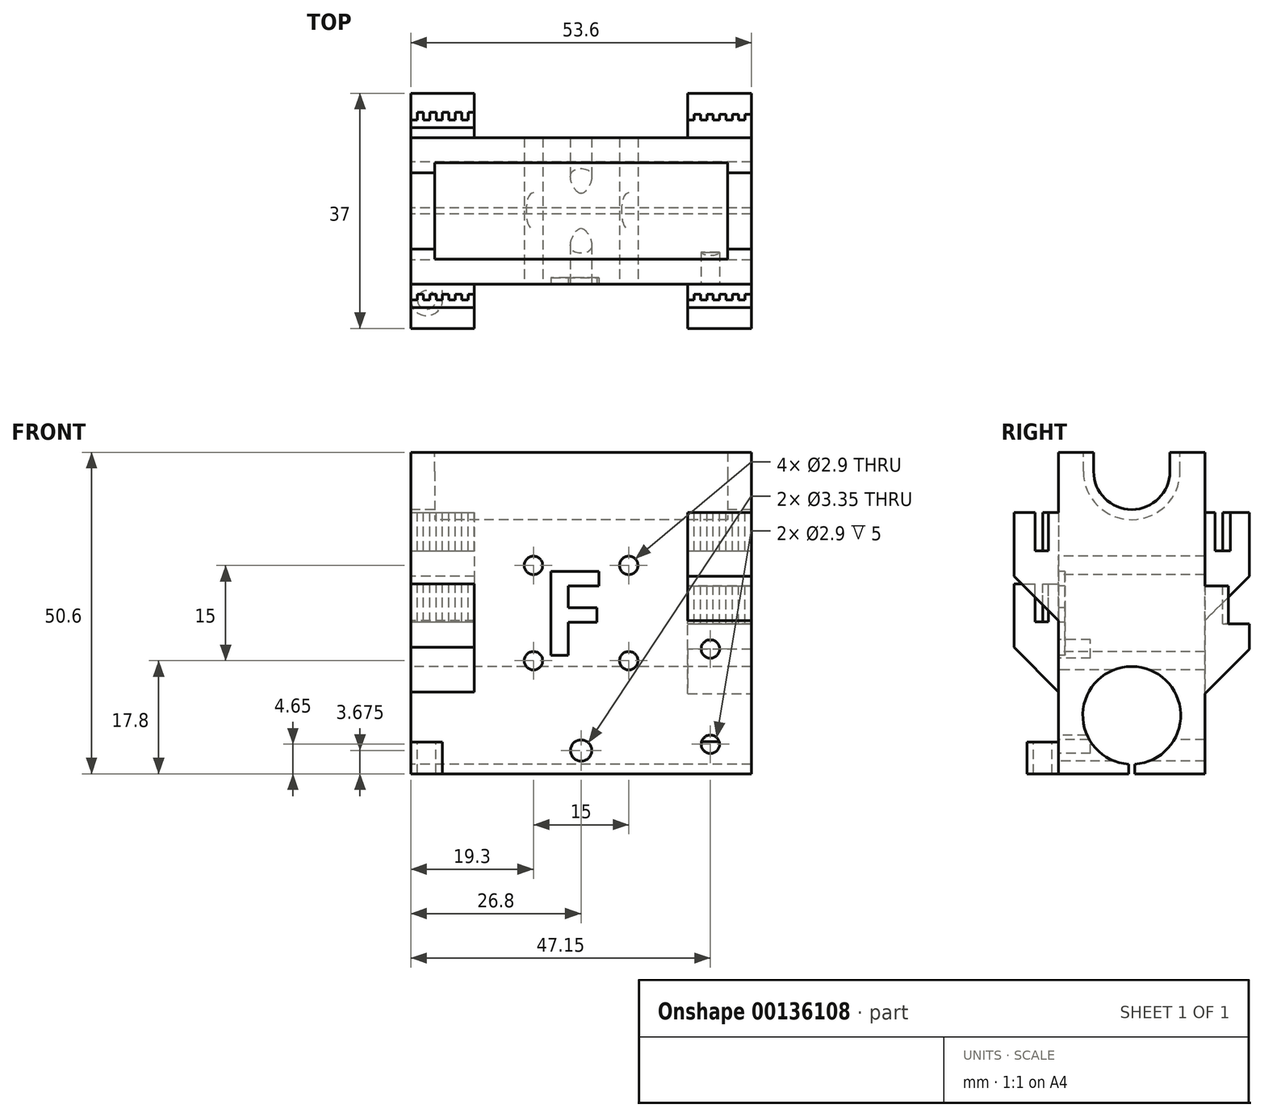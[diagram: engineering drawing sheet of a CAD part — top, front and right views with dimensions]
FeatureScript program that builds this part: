
annotation { "Feature Type Name" : "Feature", "Feature Type Description" : "" }
export const myFeature = defineFeature(function(context is Context, id is Id, definition is map)
    precondition{}
    {
        {
            assignVariable(context, id + "F0", {"name" : "LM8LUU", "anyValue" : 1.8});
        }
        {
            var Q0;
            Q0=qCreatedBy(makeId("Top.planeOp"),FACE);
            var sketch = newSketch(context, id + "F1", { "sketchPlane" : qUnion([Q0])});
            skLineSegment(sketch, "E0.bottom", {"start": v(0, 0) * mm, "end": v(53.6, 0) * mm});
            skLineSegment(sketch, "E0.top", {"start": v(0, 23) * mm, "end": v(53.6, 23) * mm});
            skLineSegment(sketch, "E0.left", {"start": v(0, 0) * mm, "end": v(0, 23) * mm});
            skLineSegment(sketch, "E0.right", {"start": v(53.6, 0) * mm, "end": v(53.6, 23) * mm});
            skSolve(sketch);
        }
        {
            var Q0;
            Q0=qSketchRegion(id+"F1",true);
            extrude(context, id + "F2", {"entities" : qUnion([Q0]), "depth" : 50.6 * mm});
        }
        {
            var Q0;
            Q0=makeQuery(id+"F2.opExtrude","SWEPT_FACE",FACE,{"disambiguationData":[OSD([sQuery(id+"F1.wireOp",EDGE,"E0.left")])]});
            var sketch = newSketch(context, id + "F3", { "sketchPlane" : qUnion([Q0])});
            skCircle(sketch, "E1", {"center": v(-11.5, 9.2) * mm, "radius": 7.7 * mm});
            skCircle(sketch, "E2", {"center": v(-11.5, 47.6) * mm, "radius": 6 * mm});
            skLineSegment(sketch, "E3", {"start": v(-23, 47.6) * mm, "end": v(0, 47.6) * mm, "construction": true});
            skLineSegment(sketch, "E4", {"start": v(-17.5, 50.6) * mm, "end": v(-17.5, 47.6) * mm});
            skLineSegment(sketch, "E5", {"start": v(-5.5, 50.6) * mm, "end": v(-5.5, 47.6) * mm});
            skLineSegment(sketch, "E6", {"start": v(-23, 9.2) * mm, "end": v(0, 9.2) * mm, "construction": true});
            skLineSegment(sketch, "E7", {"start": v(-11.5, 9.2) * mm, "end": v(-11.5, 0) * mm, "construction": true});
            skLineSegment(sketch, "E8", {"start": v(-11.5, 0) * mm, "end": v(-12, 0) * mm});
            skLineSegment(sketch, "E9", {"start": v(-12, 0) * mm, "end": v(-12, 1.52) * mm});
            skLineSegment(sketch, "E10", {"start": v(-12, 1.52) * mm, "end": v(-11, 1.52) * mm});
            skLineSegment(sketch, "E11", {"start": v(-11, 1.52) * mm, "end": v(-11, 0) * mm});
            skLineSegment(sketch, "E12", {"start": v(-11, 0) * mm, "end": v(-11.5, 0) * mm});
            skLineSegment(sketch, "E13", {"start": v(-11.5, 15.6) * mm, "end": v(-11.5, 16.9) * mm});
            skLineSegment(sketch, "E14", {"start": v(-11.5, 15.6) * mm, "end": v(-6.94, 15.4) * mm});
            skLineSegment(sketch, "E15", {"start": v(-11.5, 15.6) * mm, "end": v(-16.06, 15.4) * mm});
            skCircle(sketch, "E16", {"center": v(-11.5, 47.6) * mm, "radius": 7.6 * mm});
            skLineSegment(sketch, "E17", {"start": v(-3.9, 47.6) * mm, "end": v(-3.9, 50.6) * mm});
            skLineSegment(sketch, "E18", {"start": v(-19.1, 47.6) * mm, "end": v(-19.1, 50.6) * mm});
            skSolve(sketch);
        }
        {
            var Q0;
            {var subQ0=sQuery(id+"F3.wireOp",EDGE,"E14");var subQ1=sQuery(id+"F3.wireOp",EDGE,"E1");var subQ3=makeQuery(id+"F3.imprint","INTERSECT",VERTEX,{"disambiguationData":[OD(0.0)],"derivedFrom":[subQ1,subQ0]});Q0=makeQuery(id+"F3.imprint","IMPRINT",FACE,{"disambiguationData":[TD([[makeQuery(id+"F3.imprint","IMPRINT",EDGE,{"disambiguationData":[TD([[subQ3,-1.0]])],"derivedFrom":subQ1}),1.0]])]});}
            var Q1;
            {var subQ0=sQuery(id+"F3.wireOp",EDGE,"E15");var subQ1=sQuery(id+"F3.wireOp",EDGE,"E1");var subQ3=makeQuery(id+"F3.imprint","INTERSECT",VERTEX,{"disambiguationData":[OD(0.0)],"derivedFrom":[subQ1,subQ0]});Q1=makeQuery(id+"F3.imprint","IMPRINT",FACE,{"disambiguationData":[TD([[makeQuery(id+"F3.imprint","IMPRINT",EDGE,{"disambiguationData":[TD([[subQ3,1.0]])],"derivedFrom":subQ1}),1.0]])]});}
            var Q2;
            Q2=makeQuery(id+"F3.imprint","IMPRINT",FACE,{"disambiguationData":[TD([[makeQuery(id+"F3.imprint","IMPRINT",EDGE,{"derivedFrom":sQuery(id+"F3.wireOp",EDGE,"E8")}),-1.0]])]});
            var Q3;
            {var subQ0=sQuery(id+"F3.wireOp",EDGE,"E10");Q3=makeQuery(id+"F3.imprint","IMPRINT",FACE,{"disambiguationData":[TD([[makeQuery(id+"F3.imprint","IMPRINT",EDGE,{"derivedFrom":subQ0}),-1.0]])]});}
            var Q4;
            {var subQ3=sQuery(id+"F3.wireOp",EDGE,"E13");Q4=makeQuery(id+"F3.imprint","IMPRINT",FACE,{"disambiguationData":[TD([[makeQuery(id+"F3.imprint","IMPRINT",EDGE,{"derivedFrom":subQ3}),-1.0]])]});}
            var Q5;
            {var subQ3=sQuery(id+"F3.wireOp",EDGE,"E13");Q5=makeQuery(id+"F3.imprint","IMPRINT",FACE,{"disambiguationData":[TD([[makeQuery(id+"F3.imprint","IMPRINT",EDGE,{"derivedFrom":subQ3}),1.0]])]});}
            var Q6;
            {var subQ7=sQuery(id+"F3.wireOp",EDGE,"E10");Q6=makeQuery(id+"F3.imprint","IMPRINT",FACE,{"disambiguationData":[TD([[makeQuery(id+"F3.imprint","IMPRINT",EDGE,{"derivedFrom":subQ7}),1.0]])]});}
            var Q7;
            {var subQ3=sQuery(id+"F3.wireOp",EDGE,"E5");Q7=makeQuery(id+"F3.imprint","IMPRINT",FACE,{"disambiguationData":[TD([[makeQuery(id+"F3.imprint","IMPRINT",EDGE,{"derivedFrom":subQ3}),-1.0]])]});}
            var Q8;
            {var subQ0=sQuery(id+"F3.wireOp",EDGE,"E4");Q8=makeQuery(id+"F3.imprint","IMPRINT",FACE,{"disambiguationData":[TD([[makeQuery(id+"F3.imprint","IMPRINT",EDGE,{"derivedFrom":subQ0}),1.0]])]});}
            var Q9;
            {var subQ0=sQuery(id+"F3.wireOp",EDGE,"E4");Q9=makeQuery(id+"F3.imprint","IMPRINT",FACE,{"disambiguationData":[TD([[makeQuery(id+"F3.imprint","IMPRINT",EDGE,{"derivedFrom":subQ0}),1.0]])]});}
            var Q10;
            {var subQ3=sQuery(id+"F3.wireOp",EDGE,"E5");Q10=makeQuery(id+"F3.imprint","IMPRINT",FACE,{"disambiguationData":[TD([[makeQuery(id+"F3.imprint","IMPRINT",EDGE,{"derivedFrom":subQ3}),-1.0]])]});}
            var Q11;
            {var subQ1=sQuery(id+"F3.wireOp",EDGE,"E2");var subQ4=makeQuery(id+"F3.imprint","INTERSECT",VERTEX,{"derivedFrom":[subQ1,sQuery(id+"F3.wireOp",EDGE,"E5")]});Q11=makeQuery(id+"F3.imprint","IMPRINT",FACE,{"disambiguationData":[TD([[makeQuery(id+"F3.imprint","IMPRINT",EDGE,{"disambiguationData":[TD([[subQ4,-1.0]])],"derivedFrom":subQ1}),1.0]])]});}
            extrude(context, id + "F4", {"entities" : qUnion([Q0, Q1, Q2, Q3, Q4, Q5, Q6, Q7, Q8, Q9, Q10, Q11]), "operationType" : NewBodyOperationType.REMOVE, "endBound" : BoundingType.THROUGH_ALL, "oppositeDirection" : true, "depth" : 25 * mm});
        }
        {
            var Q0;
            {var subQ3=sQuery(id+"F3.wireOp",EDGE,"E4");Q0=makeQuery(id+"F3.imprint","IMPRINT",FACE,{"disambiguationData":[TD([[makeQuery(id+"F3.imprint","IMPRINT",EDGE,{"derivedFrom":subQ3}),-1.0]])]});}
            var Q1;
            {var subQ3=sQuery(id+"F3.wireOp",EDGE,"E18");Q1=makeQuery(id+"F3.imprint","IMPRINT",FACE,{"disambiguationData":[TD([[makeQuery(id+"F3.imprint","IMPRINT",EDGE,{"derivedFrom":subQ3}),-1.0]])]});}
            var Q2;
            {var subQ3=sQuery(id+"F3.wireOp",EDGE,"E17");Q2=makeQuery(id+"F3.imprint","IMPRINT",FACE,{"disambiguationData":[TD([[makeQuery(id+"F3.imprint","IMPRINT",EDGE,{"derivedFrom":subQ3}),1.0]])]});}
            extrude(context, id + "F5", {"entities" : qUnion([Q0, Q1, Q2]), "operationType" : NewBodyOperationType.REMOVE, "oppositeDirection" : true, "depth" : (46.25 + getVariable(context, 'LM8LUU') * 2) * mm});
        }
        {
            var Q0;
            {var subQ3=sQuery(id+"F3.wireOp",EDGE,"E4");Q0=makeQuery(id+"F3.imprint","IMPRINT",FACE,{"disambiguationData":[TD([[makeQuery(id+"F3.imprint","IMPRINT",EDGE,{"derivedFrom":subQ3}),-1.0]])]});}
            var Q1;
            {var subQ3=sQuery(id+"F3.wireOp",EDGE,"E18");Q1=makeQuery(id+"F3.imprint","IMPRINT",FACE,{"disambiguationData":[TD([[makeQuery(id+"F3.imprint","IMPRINT",EDGE,{"derivedFrom":subQ3}),-1.0]])]});}
            var Q2;
            {var subQ3=sQuery(id+"F3.wireOp",EDGE,"E17");Q2=makeQuery(id+"F3.imprint","IMPRINT",FACE,{"disambiguationData":[TD([[makeQuery(id+"F3.imprint","IMPRINT",EDGE,{"derivedFrom":subQ3}),1.0]])]});}
            extrude(context, id + "F6", {"entities" : qUnion([Q0, Q1, Q2]), "operationType" : NewBodyOperationType.ADD, "oppositeDirection" : true, "depth" : (26.75 - getVariable(context, 'LM8LUU')) * mm});
        }
        {
            var Q0;
            {var subQ3=sQuery(id+"F3.wireOp",EDGE,"E4");Q0=makeQuery(id+"F3.imprint","IMPRINT",FACE,{"disambiguationData":[TD([[makeQuery(id+"F3.imprint","IMPRINT",EDGE,{"derivedFrom":subQ3}),-1.0]])]});}
            var Q1;
            {var subQ3=sQuery(id+"F3.wireOp",EDGE,"E18");Q1=makeQuery(id+"F3.imprint","IMPRINT",FACE,{"disambiguationData":[TD([[makeQuery(id+"F3.imprint","IMPRINT",EDGE,{"derivedFrom":subQ3}),-1.0]])]});}
            var Q2;
            {var subQ3=sQuery(id+"F3.wireOp",EDGE,"E17");Q2=makeQuery(id+"F3.imprint","IMPRINT",FACE,{"disambiguationData":[TD([[makeQuery(id+"F3.imprint","IMPRINT",EDGE,{"derivedFrom":subQ3}),1.0]])]});}
            extrude(context, id + "F7", {"entities" : qUnion([Q0, Q1, Q2]), "operationType" : NewBodyOperationType.REMOVE, "oppositeDirection" : true, "depth" : (23.25 + getVariable(context, 'LM8LUU')) * mm});
        }
        {
            var Q0;
            {var subQ3=sQuery(id+"F3.wireOp",EDGE,"E4");Q0=makeQuery(id+"F3.imprint","IMPRINT",FACE,{"disambiguationData":[TD([[makeQuery(id+"F3.imprint","IMPRINT",EDGE,{"derivedFrom":subQ3}),-1.0]])]});}
            var Q1;
            {var subQ3=sQuery(id+"F3.wireOp",EDGE,"E18");Q1=makeQuery(id+"F3.imprint","IMPRINT",FACE,{"disambiguationData":[TD([[makeQuery(id+"F3.imprint","IMPRINT",EDGE,{"derivedFrom":subQ3}),-1.0]])]});}
            var Q2;
            {var subQ3=sQuery(id+"F3.wireOp",EDGE,"E17");Q2=makeQuery(id+"F3.imprint","IMPRINT",FACE,{"disambiguationData":[TD([[makeQuery(id+"F3.imprint","IMPRINT",EDGE,{"derivedFrom":subQ3}),1.0]])]});}
            extrude(context, id + "F8", {"entities" : qUnion([Q0, Q1, Q2]), "operationType" : NewBodyOperationType.ADD, "oppositeDirection" : true, "depth" : 3.75 * mm});
        }
        {
            var Q0;
            Q0=makeQuery(id+"F2.opExtrude","SWEPT_FACE",FACE,{"disambiguationData":[OSD([sQuery(id+"F1.wireOp",EDGE,"E0.bottom")])]});
            var sketch = newSketch(context, id + "F9", { "sketchPlane" : qUnion([Q0])});
            skLineSegment(sketch, "E19.bottom", {"start": v(0, 29.9) * mm, "end": v(10, 29.9) * mm});
            skLineSegment(sketch, "E19.top", {"start": v(0, 9.9) * mm, "end": v(10, 9.9) * mm});
            skLineSegment(sketch, "E19.left", {"start": v(0, 29.9) * mm, "end": v(0, 9.9) * mm});
            skLineSegment(sketch, "E19.right", {"start": v(10, 29.9) * mm, "end": v(10, 9.9) * mm});
            skLineSegment(sketch, "E20.bottom", {"start": v(53.6, 41.1) * mm, "end": v(43.6, 41.1) * mm});
            skLineSegment(sketch, "E20.top", {"start": v(53.6, 21.1) * mm, "end": v(43.6, 21.1) * mm});
            skLineSegment(sketch, "E20.left", {"start": v(53.6, 41.1) * mm, "end": v(53.6, 21.1) * mm});
            skLineSegment(sketch, "E20.right", {"start": v(43.6, 41.1) * mm, "end": v(43.6, 21.1) * mm});
            skPoint(sketch, "E21", {"position": v(0, 47.6) * mm});
            skPoint(sketch, "E22", {"position": v(0, 9.4) * mm});
            skSolve(sketch);
        }
        {
            var Q0;
            Q0=qSketchRegion(id+"F9",true);
            extrude(context, id + "F10", {"entities" : qUnion([Q0]), "operationType" : NewBodyOperationType.ADD, "depth" : 7 * mm});
        }
        {
            var Q0;
            Q0=makeQuery(id+"F10.opExtrude","CAP_EDGE",EDGE,{"disambiguationData":[OSD([sQuery(id+"F9.wireOp",EDGE,"E19.top")])],"isStart":false});
            var Q1;
            Q1=makeQuery(id+"F10.opExtrude","CAP_EDGE",EDGE,{"disambiguationData":[OSD([sQuery(id+"F9.wireOp",EDGE,"E20.top")])],"isStart":false});
            chamfer(context, id + "F11", {"entities" : qUnion([Q0, Q1]), "width" : 10 * mm, "tangentPropagation" : true});
        }
        {
            var Q0;
            Q0=makeQuery(id+"F10.opExtrude","SWEPT_FACE",FACE,{"disambiguationData":[OSD([sQuery(id+"F9.wireOp",EDGE,"E19.bottom")])]});
            var sketch = newSketch(context, id + "F12", { "sketchPlane" : qUnion([Q0])});
            skLineSegment(sketch, "E23.left", {"start": v(0, -3.7) * mm, "end": v(0, -1.6) * mm});
            skLineSegment(sketch, "E24", {"start": v(6, -2.5) * mm, "end": v(7, -2.5) * mm});
            skLineSegment(sketch, "E25", {"start": v(4, -2.5) * mm, "end": v(5, -2.5) * mm});
            skLineSegment(sketch, "E26", {"start": v(0, -2.5) * mm, "end": v(1, -2.5) * mm});
            skLineSegment(sketch, "E27", {"start": v(7, -1.6) * mm, "end": v(8, -1.6) * mm});
            skLineSegment(sketch, "E28", {"start": v(2, -2.5) * mm, "end": v(3, -2.5) * mm});
            skLineSegment(sketch, "E29", {"start": v(3, -1.6) * mm, "end": v(4, -1.6) * mm});
            skLineSegment(sketch, "E30", {"start": v(8, -2.5) * mm, "end": v(9, -2.5) * mm});
            skLineSegment(sketch, "E31", {"start": v(8, -1.6) * mm, "end": v(8, -2.5) * mm});
            skLineSegment(sketch, "E32", {"start": v(9, -2.5) * mm, "end": v(9, -1.6) * mm});
            skLineSegment(sketch, "E33", {"start": v(10, -1.6) * mm, "end": v(10, -2.5) * mm});
            skLineSegment(sketch, "E34", {"start": v(6, -1.6) * mm, "end": v(6, -2.5) * mm});
            skLineSegment(sketch, "E35", {"start": v(2, -1.6) * mm, "end": v(2, -2.5) * mm});
            skLineSegment(sketch, "E36", {"start": v(1, -1.6) * mm, "end": v(2, -1.6) * mm});
            skLineSegment(sketch, "E37", {"start": v(1, -2.5) * mm, "end": v(1, -1.6) * mm});
            skLineSegment(sketch, "E38", {"start": v(9, -1.6) * mm, "end": v(10, -1.6) * mm});
            skLineSegment(sketch, "E39", {"start": v(5, -1.6) * mm, "end": v(6, -1.6) * mm});
            skLineSegment(sketch, "E40", {"start": v(5, -2.5) * mm, "end": v(5, -1.6) * mm});
            skLineSegment(sketch, "E41", {"start": v(3, -2.5) * mm, "end": v(3, -1.6) * mm});
            skLineSegment(sketch, "E42", {"start": v(4, -1.6) * mm, "end": v(4, -2.5) * mm});
            skLineSegment(sketch, "E43", {"start": v(7, -2.5) * mm, "end": v(7, -1.6) * mm});
            skLineSegment(sketch, "E44", {"start": v(0, -1.6) * mm, "end": v(0, -2.5) * mm});
            skLineSegment(sketch, "E45", {"start": v(10, -2.5) * mm, "end": v(10, -3.7) * mm});
            skLineSegment(sketch, "E46", {"start": v(0, -3.7) * mm, "end": v(10, -3.7) * mm});
            skLineSegment(sketch, "E47", {"start": v(5.3, -1.6) * mm, "end": v(5.3, 0) * mm});
            skSolve(sketch);
        }
        {
            var Q0;
            Q0=qSketchRegion(id+"F12",true);
            extrude(context, id + "F13", {"entities" : qUnion([Q0]), "operationType" : NewBodyOperationType.REMOVE, "oppositeDirection" : true, "depth" : 6 * mm});
        }
        {
            var Q0;
            Q0=makeQuery(id+"F10.opExtrude","SWEPT_FACE",FACE,{"disambiguationData":[OSD([sQuery(id+"F9.wireOp",EDGE,"E20.bottom")])]});
            var sketch = newSketch(context, id + "F14", { "sketchPlane" : qUnion([Q0])});
            skLineSegment(sketch, "E48.left", {"start": v(43.6, -3.7) * mm, "end": v(43.6, -1.6) * mm});
            skLineSegment(sketch, "E49", {"start": v(49.6, -2.5) * mm, "end": v(50.6, -2.5) * mm});
            skLineSegment(sketch, "E50", {"start": v(47.6, -2.5) * mm, "end": v(48.6, -2.5) * mm});
            skLineSegment(sketch, "E51", {"start": v(43.6, -2.5) * mm, "end": v(44.6, -2.5) * mm});
            skLineSegment(sketch, "E52", {"start": v(50.6, -1.6) * mm, "end": v(51.6, -1.6) * mm});
            skLineSegment(sketch, "E53", {"start": v(45.6, -2.5) * mm, "end": v(46.6, -2.5) * mm});
            skLineSegment(sketch, "E54", {"start": v(46.6, -1.6) * mm, "end": v(47.6, -1.6) * mm});
            skLineSegment(sketch, "E55", {"start": v(51.6, -2.5) * mm, "end": v(52.6, -2.5) * mm});
            skLineSegment(sketch, "E56", {"start": v(51.6, -1.6) * mm, "end": v(51.6, -2.5) * mm});
            skLineSegment(sketch, "E57", {"start": v(52.6, -2.5) * mm, "end": v(52.6, -1.6) * mm});
            skLineSegment(sketch, "E58", {"start": v(53.6, -1.6) * mm, "end": v(53.6, -2.5) * mm});
            skLineSegment(sketch, "E59", {"start": v(49.6, -1.6) * mm, "end": v(49.6, -2.5) * mm});
            skLineSegment(sketch, "E60", {"start": v(45.6, -1.6) * mm, "end": v(45.6, -2.5) * mm});
            skLineSegment(sketch, "E61", {"start": v(44.6, -1.6) * mm, "end": v(45.6, -1.6) * mm});
            skLineSegment(sketch, "E62", {"start": v(44.6, -2.5) * mm, "end": v(44.6, -1.6) * mm});
            skLineSegment(sketch, "E63", {"start": v(52.6, -1.6) * mm, "end": v(53.6, -1.6) * mm});
            skLineSegment(sketch, "E64", {"start": v(48.6, -1.6) * mm, "end": v(49.6, -1.6) * mm});
            skLineSegment(sketch, "E65", {"start": v(48.6, -2.5) * mm, "end": v(48.6, -1.6) * mm});
            skLineSegment(sketch, "E66", {"start": v(46.6, -2.5) * mm, "end": v(46.6, -1.6) * mm});
            skLineSegment(sketch, "E67", {"start": v(47.6, -1.6) * mm, "end": v(47.6, -2.5) * mm});
            skLineSegment(sketch, "E68", {"start": v(50.6, -2.5) * mm, "end": v(50.6, -1.6) * mm});
            skLineSegment(sketch, "E69", {"start": v(43.6, -1.6) * mm, "end": v(43.6, -2.5) * mm});
            skLineSegment(sketch, "E70", {"start": v(53.6, -2.5) * mm, "end": v(53.6, -3.7) * mm});
            skLineSegment(sketch, "E71", {"start": v(43.6, -3.7) * mm, "end": v(53.6, -3.7) * mm});
            skLineSegment(sketch, "E72", {"start": v(48.83, -1.6) * mm, "end": v(48.83, 0) * mm});
            skSolve(sketch);
        }
        {
            var Q0;
            Q0=qSketchRegion(id+"F14",true);
            extrude(context, id + "F15", {"entities" : qUnion([Q0]), "operationType" : NewBodyOperationType.REMOVE, "oppositeDirection" : true, "depth" : 6 * mm});
        }
        {
            var Q0;
            Q0=makeQuery(id+"F2.opExtrude","SWEPT_FACE",FACE,{"disambiguationData":[OSD([sQuery(id+"F1.wireOp",EDGE,"E0.top")])]});
            var sketch = newSketch(context, id + "F16", { "sketchPlane" : qUnion([Q0])});
            skLineSegment(sketch, "E73.bottom", {"start": v(-53.6, 9.6) * mm, "end": v(-43.6, 9.6) * mm});
            skLineSegment(sketch, "E73.top", {"start": v(-53.6, 29.6) * mm, "end": v(-43.6, 29.6) * mm});
            skLineSegment(sketch, "E73.left", {"start": v(-53.6, 9.6) * mm, "end": v(-53.6, 29.6) * mm});
            skLineSegment(sketch, "E73.right", {"start": v(-43.6, 9.6) * mm, "end": v(-43.6, 29.6) * mm});
            skLineSegment(sketch, "E74.bottom", {"start": v(0, 41.1) * mm, "end": v(-10, 41.1) * mm});
            skLineSegment(sketch, "E74.top", {"start": v(0, 21.1) * mm, "end": v(-10, 21.1) * mm});
            skLineSegment(sketch, "E74.left", {"start": v(0, 41.1) * mm, "end": v(0, 21.1) * mm});
            skLineSegment(sketch, "E74.right", {"start": v(-10, 41.1) * mm, "end": v(-10, 21.1) * mm});
            skSolve(sketch);
        }
        {
            var Q0;
            Q0=qSketchRegion(id+"F16",true);
            extrude(context, id + "F17", {"entities" : qUnion([Q0]), "operationType" : NewBodyOperationType.ADD, "depth" : 7 * mm});
        }
        {
            var Q0;
            Q0=makeQuery(id+"F17.opExtrude","SWEPT_FACE",FACE,{"disambiguationData":[OSD([sQuery(id+"F16.wireOp",EDGE,"E73.top")])]});
            var sketch = newSketch(context, id + "F18", { "sketchPlane" : qUnion([Q0])});
            skLineSegment(sketch, "E75.left", {"start": v(43.6, 24.6) * mm, "end": v(43.6, 26.7) * mm});
            skLineSegment(sketch, "E76", {"start": v(49.6, 25.8) * mm, "end": v(50.6, 25.8) * mm});
            skLineSegment(sketch, "E77", {"start": v(47.6, 25.8) * mm, "end": v(48.6, 25.8) * mm});
            skLineSegment(sketch, "E78", {"start": v(43.6, 25.8) * mm, "end": v(44.6, 25.8) * mm});
            skLineSegment(sketch, "E79", {"start": v(50.6, 26.7) * mm, "end": v(51.6, 26.7) * mm});
            skLineSegment(sketch, "E80", {"start": v(45.6, 25.8) * mm, "end": v(46.6, 25.8) * mm});
            skLineSegment(sketch, "E81", {"start": v(46.6, 26.7) * mm, "end": v(47.6, 26.7) * mm});
            skLineSegment(sketch, "E82", {"start": v(51.6, 25.8) * mm, "end": v(52.6, 25.8) * mm});
            skLineSegment(sketch, "E83", {"start": v(51.6, 26.7) * mm, "end": v(51.6, 25.8) * mm});
            skLineSegment(sketch, "E84", {"start": v(52.6, 25.8) * mm, "end": v(52.6, 26.7) * mm});
            skLineSegment(sketch, "E85", {"start": v(53.6, 26.7) * mm, "end": v(53.6, 25.8) * mm});
            skLineSegment(sketch, "E86", {"start": v(49.6, 26.7) * mm, "end": v(49.6, 25.8) * mm});
            skLineSegment(sketch, "E87", {"start": v(45.6, 26.7) * mm, "end": v(45.6, 25.8) * mm});
            skLineSegment(sketch, "E88", {"start": v(44.6, 26.7) * mm, "end": v(45.6, 26.7) * mm});
            skLineSegment(sketch, "E89", {"start": v(44.6, 25.8) * mm, "end": v(44.6, 26.7) * mm});
            skLineSegment(sketch, "E90", {"start": v(52.6, 26.7) * mm, "end": v(53.6, 26.7) * mm});
            skLineSegment(sketch, "E91", {"start": v(48.6, 26.7) * mm, "end": v(49.6, 26.7) * mm});
            skLineSegment(sketch, "E92", {"start": v(48.6, 25.8) * mm, "end": v(48.6, 26.7) * mm});
            skLineSegment(sketch, "E93", {"start": v(46.6, 25.8) * mm, "end": v(46.6, 26.7) * mm});
            skLineSegment(sketch, "E94", {"start": v(47.6, 26.7) * mm, "end": v(47.6, 25.8) * mm});
            skLineSegment(sketch, "E95", {"start": v(50.6, 25.8) * mm, "end": v(50.6, 26.7) * mm});
            skLineSegment(sketch, "E96", {"start": v(43.6, 26.7) * mm, "end": v(43.6, 25.8) * mm});
            skLineSegment(sketch, "E97", {"start": v(53.6, 25.8) * mm, "end": v(53.6, 24.6) * mm});
            skLineSegment(sketch, "E98", {"start": v(43.6, 24.6) * mm, "end": v(53.6, 24.6) * mm});
            skLineSegment(sketch, "E99", {"start": v(48.6, 24.6) * mm, "end": v(48.6, 23) * mm});
            skSolve(sketch);
        }
        {
            var Q0;
            {var subQ4=sQuery(id+"F18.wireOp",EDGE,"E75.left");Q0=makeQuery(id+"F18.imprint","IMPRINT",FACE,{"disambiguationData":[TD([[makeQuery(id+"F18.imprint","IMPRINT",EDGE,{"derivedFrom":subQ4}),1.0]])]});}
            extrude(context, id + "F19", {"entities" : qUnion([Q0]), "operationType" : NewBodyOperationType.REMOVE, "oppositeDirection" : true, "depth" : 6 * mm});
        }
        {
            var Q0;
            Q0=makeQuery(id+"F17.opExtrude","SWEPT_FACE",FACE,{"disambiguationData":[OSD([sQuery(id+"F16.wireOp",EDGE,"E74.bottom")])]});
            var sketch = newSketch(context, id + "F20", { "sketchPlane" : qUnion([Q0])});
            skLineSegment(sketch, "E100", {"start": v(6, 25.8) * mm, "end": v(7, 25.8) * mm});
            skLineSegment(sketch, "E101", {"start": v(4, 25.8) * mm, "end": v(5, 25.8) * mm});
            skLineSegment(sketch, "E102", {"start": v(0, 25.8) * mm, "end": v(1, 25.8) * mm});
            skLineSegment(sketch, "E103", {"start": v(7, 27) * mm, "end": v(8, 27) * mm});
            skLineSegment(sketch, "E104", {"start": v(2, 25.8) * mm, "end": v(3, 25.8) * mm});
            skLineSegment(sketch, "E105", {"start": v(3, 27) * mm, "end": v(4, 27) * mm});
            skLineSegment(sketch, "E106", {"start": v(8, 25.8) * mm, "end": v(9, 25.8) * mm});
            skLineSegment(sketch, "E107", {"start": v(8, 27) * mm, "end": v(8, 25.8) * mm});
            skLineSegment(sketch, "E108", {"start": v(9, 25.8) * mm, "end": v(9, 27) * mm});
            skLineSegment(sketch, "E109", {"start": v(10, 27) * mm, "end": v(10, 25.8) * mm});
            skLineSegment(sketch, "E110", {"start": v(6, 27) * mm, "end": v(6, 25.8) * mm});
            skLineSegment(sketch, "E111", {"start": v(2, 27) * mm, "end": v(2, 25.8) * mm});
            skLineSegment(sketch, "E112", {"start": v(1, 27) * mm, "end": v(2, 27) * mm});
            skLineSegment(sketch, "E113", {"start": v(1, 25.8) * mm, "end": v(1, 27) * mm});
            skLineSegment(sketch, "E114", {"start": v(9, 27) * mm, "end": v(10, 27) * mm});
            skLineSegment(sketch, "E115", {"start": v(5, 27) * mm, "end": v(6, 27) * mm});
            skLineSegment(sketch, "E116", {"start": v(5, 25.8) * mm, "end": v(5, 27) * mm});
            skLineSegment(sketch, "E117", {"start": v(3, 25.8) * mm, "end": v(3, 27) * mm});
            skLineSegment(sketch, "E118", {"start": v(4, 27) * mm, "end": v(4, 25.8) * mm});
            skLineSegment(sketch, "E119", {"start": v(7, 25.8) * mm, "end": v(7, 27) * mm});
            skLineSegment(sketch, "E120", {"start": v(10, 25.8) * mm, "end": v(10, 24.6) * mm});
            skLineSegment(sketch, "E121", {"start": v(0, 24.6) * mm, "end": v(10, 24.6) * mm});
            skLineSegment(sketch, "E122", {"start": v(5, 24.6) * mm, "end": v(5, 23) * mm});
            skLineSegment(sketch, "E123", {"start": v(0, 24.6) * mm, "end": v(0, 25.8) * mm});
            skSolve(sketch);
        }
        {
            var Q0;
            Q0=makeQuery(id+"F20.imprint","IMPRINT",FACE,{"disambiguationData":[TD([[makeQuery(id+"F20.imprint","IMPRINT",EDGE,{"derivedFrom":sQuery(id+"F20.wireOp",EDGE,"E100")}),-1.0]])]});
            extrude(context, id + "F21", {"entities" : qUnion([Q0]), "operationType" : NewBodyOperationType.REMOVE, "oppositeDirection" : true, "depth" : 6 * mm});
        }
        {
            var Q0;
            Q0=makeQuery(id+"F17.opExtrude","CAP_EDGE",EDGE,{"disambiguationData":[OSD([sQuery(id+"F16.wireOp",EDGE,"E74.top")])],"isStart":false});
            var Q1;
            Q1=makeQuery(id+"F17.opExtrude","CAP_EDGE",EDGE,{"disambiguationData":[OSD([sQuery(id+"F16.wireOp",EDGE,"E73.bottom")])],"isStart":false});
            chamfer(context, id + "F22", {"entities" : qUnion([Q0, Q1]), "width" : 10 * mm, "tangentPropagation" : true});
        }
        {
            var Q0;
            Q0=makeQuery(id+"F2.opExtrude","SWEPT_FACE",FACE,{"disambiguationData":[OSD([sQuery(id+"F1.wireOp",EDGE,"E0.bottom")])]});
            var sketch = newSketch(context, id + "F23", { "sketchPlane" : qUnion([Q0])});
            skCircle(sketch, "E124", {"center": v(19.3, 32.8) * mm, "radius": 1.45 * mm});
            skCircle(sketch, "E125", {"center": v(34.3, 32.8) * mm, "radius": 1.45 * mm});
            skCircle(sketch, "E126", {"center": v(19.3, 17.8) * mm, "radius": 1.45 * mm});
            skCircle(sketch, "E127", {"center": v(34.3, 17.8) * mm, "radius": 1.45 * mm});
            skLineSegment(sketch, "E128", {"start": v(19.3, 32.8) * mm, "end": v(0, 32.8) * mm});
            skLineSegment(sketch, "E129", {"start": v(34.3, 17.8) * mm, "end": v(53.6, 17.8) * mm});
            skLineSegment(sketch, "E130", {"start": v(34.3, 32.8) * mm, "end": v(34.3, 50.6) * mm});
            skLineSegment(sketch, "E131", {"start": v(19.3, 17.8) * mm, "end": v(19.3, 0) * mm});
            skCircle(sketch, "E132", {"center": v(26.8, 3.68) * mm, "radius": 1.68 * mm});
            skLineSegment(sketch, "E133", {"start": v(26.8, 0) * mm, "end": v(26.8, 13.82) * mm, "construction": true});
            skSolve(sketch);
        }
        {
            var Q0;
            Q0=qSketchRegion(id+"F23",true);
            var Q1;
            Q1=makeQuery(id+"F23.imprint","IMPRINT",FACE,{"disambiguationData":[TD([[makeQuery(id+"F23.imprint","IMPRINT",EDGE,{"derivedFrom":sQuery(id+"F23.wireOp",EDGE,"E124")}),1.0]])]});
            var Q2;
            Q2=makeQuery(id+"F23.imprint","IMPRINT",FACE,{"disambiguationData":[TD([[makeQuery(id+"F23.imprint","IMPRINT",EDGE,{"derivedFrom":sQuery(id+"F23.wireOp",EDGE,"E125")}),1.0]])]});
            var Q3;
            Q3=makeQuery(id+"F23.imprint","IMPRINT",FACE,{"disambiguationData":[TD([[makeQuery(id+"F23.imprint","IMPRINT",EDGE,{"derivedFrom":sQuery(id+"F23.wireOp",EDGE,"E127")}),1.0]])]});
            var Q4;
            Q4=makeQuery(id+"F23.imprint","IMPRINT",FACE,{"disambiguationData":[TD([[makeQuery(id+"F23.imprint","IMPRINT",EDGE,{"derivedFrom":sQuery(id+"F23.wireOp",EDGE,"E126")}),1.0]])]});
            extrude(context, id + "F24", {"entities" : qUnion([Q0, Q1, Q2, Q3, Q4]), "operationType" : NewBodyOperationType.REMOVE, "endBound" : BoundingType.THROUGH_ALL, "oppositeDirection" : true, "depth" : 25 * mm});
        }
        {
            var Q0;
            Q0=makeQuery(id+"F2.opExtrude","SWEPT_FACE",FACE,{"disambiguationData":[OSD([sQuery(id+"F1.wireOp",EDGE,"E0.bottom")])]});
            var sketch = newSketch(context, id + "F25", { "sketchPlane" : qUnion([Q0])});
            skCircle(sketch, "E134", {"center": v(47.15, 19.65) * mm, "radius": 1.45 * mm});
            skCircle(sketch, "E135", {"center": v(47.15, 4.65) * mm, "radius": 1.45 * mm});
            skSolve(sketch);
        }
        {
            var Q0;
            Q0=qSketchRegion(id+"F25",true);
            extrude(context, id + "F26", {"entities" : qUnion([Q0]), "operationType" : NewBodyOperationType.REMOVE, "oppositeDirection" : true, "depth" : 5 * mm});
        }
        {
            var Q0;
            Q0=makeQuery(id+"F2.opExtrude","SWEPT_FACE",FACE,{"disambiguationData":[OSD([sQuery(id+"F1.wireOp",EDGE,"E0.bottom")])]});
            var sketch = newSketch(context, id + "F27", { "sketchPlane" : qUnion([Q0])});
            skText(sketch, "E136", { "text": "F", "fontName": "OpenSans-Bold.ttf"});
            skLineSegment(sketch, "E137", {"start": v(19.3, 32.8) * mm, "end": v(19.3, 17.8) * mm, "construction": true});
            skLineSegment(sketch, "E138", {"start": v(19.3, 17.8) * mm, "end": v(34.3, 17.8) * mm, "construction": true});
            skLineSegment(sketch, "E139", {"start": v(34.3, 17.8) * mm, "end": v(34.3, 32.8) * mm, "construction": true});
            skLineSegment(sketch, "E140", {"start": v(34.3, 32.8) * mm, "end": v(19.3, 32.8) * mm, "construction": true});
            skLineSegment(sketch, "E141", {"start": v(19.3, 25.3) * mm, "end": v(22.2, 25.3) * mm, "construction": true});
            skLineSegment(sketch, "E142", {"start": v(31.4, 25.3) * mm, "end": v(34.3, 25.3) * mm, "construction": true});
            skLineSegment(sketch, "E143", {"start": v(26.8, 18.66) * mm, "end": v(26.8, 17.8) * mm, "construction": true});
            skLineSegment(sketch, "E144", {"start": v(26.8, 32.8) * mm, "end": v(26.8, 31.94) * mm, "construction": true});
            const initialGuessF27  = {"E136": [0.0204, 0.01866, 1, 0, 0.01328]};
            skSetInitialGuess(sketch, initialGuessF27);
            skSolve(sketch);
        }
        {
            var Q0;
            Q0=qSketchRegion(id+"F27",true);
            extrude(context, id + "F28", {"entities" : qUnion([Q0]), "operationType" : NewBodyOperationType.REMOVE, "oppositeDirection" : true, "depth" : 1 * mm});
        }
        {
            var Q0;
            Q0=makeQuery(id+"F2.opExtrude","SWEPT_FACE",FACE,{"disambiguationData":[OSD([sQuery(id+"F1.wireOp",EDGE,"E0.bottom")])]});
            var sketch = newSketch(context, id + "F29", { "sketchPlane" : qUnion([Q0])});
            skLineSegment(sketch, "E145.bottom", {"start": v(0, 0) * mm, "end": v(5, 0) * mm});
            skLineSegment(sketch, "E145.top", {"start": v(0, 5) * mm, "end": v(5, 5) * mm});
            skLineSegment(sketch, "E145.left", {"start": v(0, 0) * mm, "end": v(0, 5) * mm});
            skLineSegment(sketch, "E145.right", {"start": v(5, 0) * mm, "end": v(5, 5) * mm});
            skSolve(sketch);
        }
        {
            var Q0;
            Q0=qSketchRegion(id+"F29",true);
            extrude(context, id + "F30", {"entities" : qUnion([Q0]), "operationType" : NewBodyOperationType.ADD, "depth" : 5 * mm});
        }
        {
            var Q0;
            Q0=makeQuery(id+"F30.opExtrude","SWEPT_FACE",FACE,{"disambiguationData":[OSD([sQuery(id+"F29.wireOp",EDGE,"E145.top")])]});
            var sketch = newSketch(context, id + "F31", { "sketchPlane" : qUnion([Q0])});
            skCircle(sketch, "E146", {"center": v(2.5, -2.5) * mm, "radius": 1.45 * mm});
            skLineSegment(sketch, "E147", {"start": v(0, -2.5) * mm, "end": v(5, -2.5) * mm});
            skSolve(sketch);
        }
        {
            var Q0;
            Q0=qSketchRegion(id+"F31",true);
            extrude(context, id + "F32", {"entities" : qUnion([Q0]), "operationType" : NewBodyOperationType.REMOVE, "oppositeDirection" : true, "depth" : 25 * mm});
        }
        {
            var Q0;
            Q0=makeQuery(id+"F30.opExtrude","CAP_EDGE",EDGE,{"disambiguationData":[OSD([sQuery(id+"F29.wireOp",EDGE,"E145.left")])],"isStart":false});
            var Q1;
            Q1=makeQuery(id+"F30.opExtrude","CAP_EDGE",EDGE,{"disambiguationData":[OSD([sQuery(id+"F29.wireOp",EDGE,"E145.right")])],"isStart":false});
            fillet(context, id + "F33", {"entities" : qUnion([Q0, Q1]), "radius" : 2.5 * mm, "tangentPropagation" : true, "allowEdgeOverflow" : false});
        }
    });
